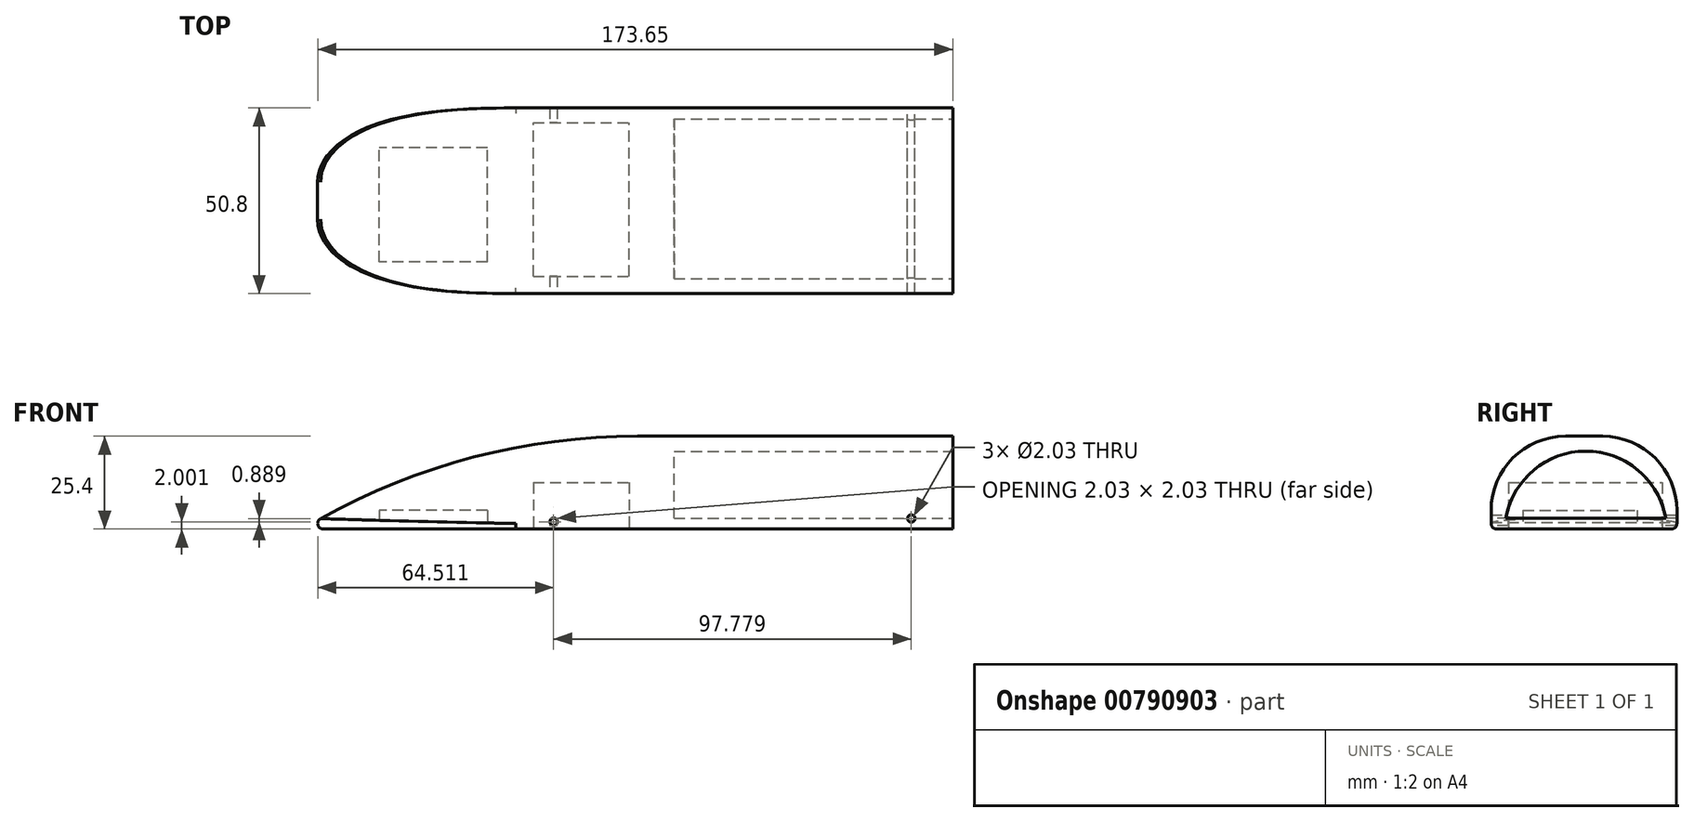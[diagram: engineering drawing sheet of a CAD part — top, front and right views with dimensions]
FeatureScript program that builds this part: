
annotation { "Feature Type Name" : "Feature", "Feature Type Description" : "" }
export const myFeature = defineFeature(function(context is Context, id is Id, definition is map)
    precondition{}
    {
        {
            var Q0;
            Q0=qCreatedBy(makeId("Top.planeOp"),FACE);
            var sketch = newSketch(context, id + "F0", { "sketchPlane" : qUnion([Q0])});
            skLineSegment(sketch, "E0.bottom", {"start": v(-88.9, -25.4) * mm, "end": v(88.9, -25.4) * mm});
            skLineSegment(sketch, "E0.top", {"start": v(-88.9, 25.4) * mm, "end": v(88.9, 25.4) * mm});
            skLineSegment(sketch, "E0.left", {"start": v(-88.9, -25.4) * mm, "end": v(-88.9, 25.4) * mm});
            skLineSegment(sketch, "E0.right", {"start": v(88.9, -25.4) * mm, "end": v(88.9, 25.4) * mm});
            skPoint(sketch, "E0.middle", {"position": v(0, 0) * mm});
            skSolve(sketch);
        }
        {
            var Q0;
            Q0=makeQuery(id+"F0.imprint","IMPRINT",FACE,{"disambiguationData":[TD([[makeQuery(id+"F0.imprint","IMPRINT",EDGE,{"derivedFrom":sQuery(id+"F0.wireOp",EDGE,"E0.bottom")}),1.0]])]});
            extrude(context, id + "F1", {"entities" : qUnion([Q0]), "depth" : 25.4 * mm, "offsetDistance" : 25.4 * mm});
        }
        {
            var Q0;
            Q0=makeQuery(id+"F1.opExtrude","CAP_EDGE",EDGE,{"disambiguationData":[OSD([sQuery(id+"F0.wireOp",EDGE,"E0.left")])],"isStart":false});
            fillet(context, id + "F2", {"entities" : qUnion([Q0]), "radius" : 177.8 * mm, "tangentPropagation" : true, "allowEdgeOverflow" : false});
        }
        {
            var Q0;
            Q0=makeQuery(id+"F2.opFillet","BLEND_EDGE",EDGE,{"blendedFrom":[makeQuery(id+"F1.opExtrude","CAP_EDGE",EDGE,{"disambiguationData":[OSD([sQuery(id+"F0.wireOp",EDGE,"E0.left")])],"isStart":false}),makeQuery(id+"F1.opExtrude","SWEPT_FACE",FACE,{"disambiguationData":[OSD([sQuery(id+"F0.wireOp",EDGE,"E0.top")])]})],"blendedInto":[makeQuery(id+"F1.opExtrude","SWEPT_FACE",FACE,{"disambiguationData":[OSD([sQuery(id+"F0.wireOp",EDGE,"E0.top")])]})]});
            var Q1;
            Q1=makeQuery(id+"F2.opFillet","BLEND_EDGE",EDGE,{"blendedFrom":[makeQuery(id+"F1.opExtrude","CAP_EDGE",EDGE,{"disambiguationData":[OSD([sQuery(id+"F0.wireOp",EDGE,"E0.left")])],"isStart":false}),makeQuery(id+"F1.opExtrude","SWEPT_FACE",FACE,{"disambiguationData":[OSD([sQuery(id+"F0.wireOp",EDGE,"E0.bottom")])]})],"blendedInto":[makeQuery(id+"F1.opExtrude","SWEPT_FACE",FACE,{"disambiguationData":[OSD([sQuery(id+"F0.wireOp",EDGE,"E0.bottom")])]})]});
            fillet(context, id + "F3", {"entities" : qUnion([Q0, Q1]), "radius" : 20.32 * mm, "tangentPropagation" : true, "allowEdgeOverflow" : false});
        }
        {
            var Q0;
            Q0=makeQuery(id+"F1.opExtrude","SWEPT_FACE",FACE,{"disambiguationData":[OSD([sQuery(id+"F0.wireOp",EDGE,"E0.right")])]});
            var sketch = newSketch(context, id + "F4", { "sketchPlane" : qUnion([Q0])});
            skLineSegment(sketch, "E1", {"start": v(-21.36, 2.9) * mm, "end": v(22.36, 2.9) * mm});
            skArc(sketch, "E2", {"start": v(22.36, 2.9) * mm, "mid": v(0.5, 21.3) * mm, "end": v(-21.36, 2.9) * mm});
            skSolve(sketch);
        }
        {
            var Q0;
            Q0=makeQuery(id+"F4.imprint","IMPRINT",FACE,{"disambiguationData":[TD([[makeQuery(id+"F4.imprint","IMPRINT",EDGE,{"derivedFrom":sQuery(id+"F4.wireOp",EDGE,"E1")}),1.0]])]});
            extrude(context, id + "F5", {"entities" : qUnion([Q0]), "operationType" : NewBodyOperationType.REMOVE, "oppositeDirection" : true, "depth" : 76.2 * mm, "offsetDistance" : 25.4 * mm});
        }
        {
            var Q0;
            Q0=makeQuery(id+"F1.opExtrude","SWEPT_FACE",FACE,{"disambiguationData":[OSD([sQuery(id+"F0.wireOp",EDGE,"E0.top")])]});
            var sketch = newSketch(context, id + "F6", { "sketchPlane" : qUnion([Q0])});
            skLineSegment(sketch, "E3", {"start": v(-1.86, 0) * mm, "end": v(-1.86, 1.27) * mm});
            skLineSegment(sketch, "E4", {"start": v(-1.86, 1.27) * mm, "end": v(-1.36, 1.27) * mm});
            skLineSegment(sketch, "E5", {"start": v(-1.36, 1.27) * mm, "end": v(-1.36, 0) * mm});
            skCircle(sketch, "E6", {"center": v(-76.77, 1.63) * mm, "radius": 1.02 * mm});
            skSolve(sketch);
        }
        {
            var Q0;
            {var subQ0=sQuery(id+"F6.wireOp",EDGE,"uXS108uW-j9nu-jN9d-v9bI-wBNLfCoZ4Cw1");Q0=makeQuery(id+"F6.imprint","IMPRINT",FACE,{"disambiguationData":[TD([[makeQuery(id+"F6.imprint","IMPRINT",EDGE,{"derivedFrom":subQ0}),-1.0]])]});}
            var Q1;
            {var subQ0=sQuery(id+"F6.wireOp",EDGE,"E3");Q1=makeQuery(id+"F6.imprint","IMPRINT",FACE,{"disambiguationData":[TD([[makeQuery(id+"F6.imprint","IMPRINT",EDGE,{"derivedFrom":subQ0}),-1.0]])]});}
            extrude(context, id + "F7", {"entities" : qUnion([Q0, Q1]), "operationType" : NewBodyOperationType.REMOVE, "oppositeDirection" : true, "depth" : 76.2 * mm, "offsetDistance" : 25.4 * mm});
        }
        {
            var Q0;
            Q0=makeQuery(id+"F7.boolean.opBoolean","COPY",FACE,{"derivedFrom":makeQuery(id+"F7.opExtrude","SWEPT_FACE",FACE,{"disambiguationData":[OSD([sQuery(id+"F6.wireOp",EDGE,"E5")])]})});
            extrude(context, id + "F8", {"entities" : qUnion([Q0]), "operationType" : NewBodyOperationType.ADD, "depth" : 25.4 * mm, "offsetDistance" : 25.4 * mm});
        }
        {
            var Q0;
            {var subQ0=sQuery(id+"F0.wireOp",EDGE,"E0.bottom");Q0=makeQuery(id+"F8.boolean.opBoolean","MERGE",FACE,{"derivedFrom":[makeQuery(id+"F1.opExtrude","SWEPT_FACE",FACE,{"disambiguationData":[OSD([subQ0])]}),makeQuery(id+"F8.opExtrude","SWEPT_FACE",FACE,{"disambiguationData":[OSD([subQ0,sQuery(id+"F6.wireOp",EDGE,"E5")])]})]});}
            var sketch = newSketch(context, id + "F9", { "sketchPlane" : qUnion([Q0])});
            skCircle(sketch, "E7", {"center": v(-20.24, 2) * mm, "radius": 1.02 * mm});
            skSolve(sketch);
        }
        {
            var Q0;
            Q0=makeQuery(id+"F9.imprint","IMPRINT",FACE,{"disambiguationData":[TD([[makeQuery(id+"F9.imprint","IMPRINT",EDGE,{"derivedFrom":sQuery(id+"F9.wireOp",EDGE,"mDFF4wp4-3rxd-4lJ0-i7Zv-oxogMf14aoRF")}),-1.0]])]});
            var Q1;
            Q1=makeQuery(id+"F9.imprint","IMPRINT",FACE,{"disambiguationData":[TD([[makeQuery(id+"F9.imprint","IMPRINT",EDGE,{"derivedFrom":sQuery(id+"F9.wireOp",EDGE,"E7")}),1.0]])]});
            extrude(context, id + "F10", {"entities" : qUnion([Q0, Q1]), "operationType" : NewBodyOperationType.REMOVE, "oppositeDirection" : true, "depth" : 76.2 * mm, "offsetDistance" : 25.4 * mm});
        }
        {
            var Q0;
            {var subQ0=makeQuery(id+"F7.opExtrude","SWEPT_FACE",FACE,{"disambiguationData":[OSD([sQuery(id+"F6.wireOp",EDGE,"6qoV6KTl-cau2-LcCE-7geX-YWWIEY5zHagg")])]});var subQ1=sQuery(id+"F6.wireOp",EDGE,"E5");var subQ2=sQuery(id+"F0.wireOp",EDGE,"E0.top");var subQ4=sQuery(id+"F0.wireOp",EDGE,"E0.bottom");var subQ6=sQuery(id+"F0.wireOp",EDGE,"E0.left");var subQ7=makeQuery(id+"F1.opExtrude","CAP_FACE",FACE,{"disambiguationData":[OSD([subQ4,subQ2,subQ6,sQuery(id+"F0.wireOp",EDGE,"E0.right")])],"isStart":true});Q0=makeQuery(id+"F10.boolean.opBoolean","SPLIT",FACE,{"disambiguationData":[TD([makeQuery(id+"F7.boolean.opBoolean","COPY",FACE,{"derivedFrom":subQ0})])],"derivedFrom":makeQuery(id+"F8.boolean.opBoolean","MERGE",FACE,{"derivedFrom":[makeQuery(id+"F7.boolean.opBoolean","SPLIT",FACE,{"disambiguationData":[TD([makeQuery(id+"F2.opFillet","BLEND_FACE",FACE,{"disambiguationData":[OSD([subQ6])]})])],"derivedFrom":subQ7}),makeQuery(id+"F7.boolean.opBoolean","SPLIT",FACE,{"disambiguationData":[TD([subQ0])],"derivedFrom":subQ7}),makeQuery(id+"F8.opExtrude","SWEPT_FACE",FACE,{"disambiguationData":[OSD([subQ2,subQ1])]})]})});}
            var sketch = newSketch(context, id + "F11", { "sketchPlane" : qUnion([Q0])});
            skLineSegment(sketch, "E8.bottom", {"start": v(-25.8, 20.65) * mm, "end": v(-5.9, 20.65) * mm});
            skLineSegment(sketch, "E8.top", {"start": v(-25.8, -21.39) * mm, "end": v(-5.9, -21.39) * mm});
            skLineSegment(sketch, "E8.left", {"start": v(-25.8, 20.65) * mm, "end": v(-25.8, -21.39) * mm});
            skLineSegment(sketch, "E8.right", {"start": v(-5.9, 20.65) * mm, "end": v(-5.9, -21.39) * mm});
            skSolve(sketch);
        }
        {
            var Q0;
            Q0=makeQuery(id+"F11.imprint","IMPRINT",FACE,{"disambiguationData":[TD([[makeQuery(id+"F11.imprint","IMPRINT",EDGE,{"derivedFrom":sQuery(id+"F11.wireOp",EDGE,"E8.bottom")}),-1.0]])]});
            extrude(context, id + "F12", {"entities" : qUnion([Q0]), "operationType" : NewBodyOperationType.REMOVE, "oppositeDirection" : true, "depth" : 12.7 * mm, "offsetDistance" : 25.4 * mm});
        }
        {
            var Q0;
            {var subQ0=sQuery(id+"F0.wireOp",EDGE,"E0.left");var subQ1=sQuery(id+"F0.wireOp",EDGE,"E0.bottom");var subQ3=makeQuery(id+"F2.opFillet","BLEND_FACE",FACE,{"disambiguationData":[OSD([subQ0])]});var subQ4=sQuery(id+"F0.wireOp",EDGE,"E0.top");var subQ6=sQuery(id+"F6.wireOp",EDGE,"E5");var subQ9=makeQuery(id+"F1.opExtrude","CAP_FACE",FACE,{"disambiguationData":[OSD([subQ1,subQ4,subQ0,sQuery(id+"F0.wireOp",EDGE,"E0.right")])],"isStart":true});Q0=makeQuery(id+"F10.boolean.opBoolean","SPLIT",FACE,{"disambiguationData":[TD([subQ3])],"derivedFrom":makeQuery(id+"F8.boolean.opBoolean","MERGE",FACE,{"derivedFrom":[makeQuery(id+"F7.boolean.opBoolean","SPLIT",FACE,{"disambiguationData":[TD([subQ3])],"derivedFrom":subQ9}),makeQuery(id+"F7.boolean.opBoolean","SPLIT",FACE,{"disambiguationData":[TD([makeQuery(id+"F7.opExtrude","SWEPT_FACE",FACE,{"disambiguationData":[OSD([sQuery(id+"F6.wireOp",EDGE,"6qoV6KTl-cau2-LcCE-7geX-YWWIEY5zHagg")])]})])],"derivedFrom":subQ9}),makeQuery(id+"F8.opExtrude","SWEPT_FACE",FACE,{"disambiguationData":[OSD([subQ4,subQ6])]})]})});}
            var sketch = newSketch(context, id + "F13", { "sketchPlane" : qUnion([Q0])});
            skLineSegment(sketch, "E9.bottom", {"start": v(-38.35, 16.72) * mm, "end": v(-67.96, 16.72) * mm});
            skLineSegment(sketch, "E9.top", {"start": v(-38.35, -14.52) * mm, "end": v(-67.96, -14.52) * mm});
            skLineSegment(sketch, "E9.left", {"start": v(-38.35, 16.72) * mm, "end": v(-38.35, -14.52) * mm});
            skLineSegment(sketch, "E9.right", {"start": v(-67.96, 16.72) * mm, "end": v(-67.96, -14.52) * mm});
            skSolve(sketch);
        }
        {
            var Q0;
            Q0=makeQuery(id+"F13.imprint","IMPRINT",FACE,{"disambiguationData":[TD([[makeQuery(id+"F13.imprint","IMPRINT",EDGE,{"derivedFrom":sQuery(id+"F13.wireOp",EDGE,"E9.bottom")}),1.0]])]});
            extrude(context, id + "F14", {"entities" : qUnion([Q0]), "operationType" : NewBodyOperationType.REMOVE, "oppositeDirection" : true, "depth" : 5.08 * mm, "offsetDistance" : 25.4 * mm});
        }
        {
            var Q0;
            Q0=makeQuery(id+"F12.boolean.opBoolean","COPY",FACE,{"derivedFrom":makeQuery(id+"F12.opExtrude","SWEPT_FACE",FACE,{"disambiguationData":[OSD([sQuery(id+"F11.wireOp",EDGE,"E8.right")])]})});
            extrude(context, id + "F15", {"entities" : qUnion([Q0]), "operationType" : NewBodyOperationType.REMOVE, "oppositeDirection" : true, "depth" : 6.35 * mm, "offsetDistance" : 25.4 * mm});
        }
        {
            var Q0;
            {var subQ0=sQuery(id+"F0.wireOp",EDGE,"E0.left");var subQ1=sQuery(id+"F0.wireOp",EDGE,"E0.top");Q0=makeQuery(id+"F3.opFillet","BLEND_EDGE",EDGE,{"blendedFrom":[makeQuery(id+"F2.opFillet","BLEND_EDGE",EDGE,{"blendedFrom":[makeQuery(id+"F1.opExtrude","CAP_EDGE",EDGE,{"disambiguationData":[OSD([subQ0])],"isStart":false}),makeQuery(id+"F1.opExtrude","SWEPT_FACE",FACE,{"disambiguationData":[OSD([subQ1])]})],"blendedInto":[makeQuery(id+"F1.opExtrude","SWEPT_FACE",FACE,{"disambiguationData":[OSD([subQ1])]})]}),makeQuery(id+"F1.opExtrude","CAP_FACE",FACE,{"disambiguationData":[OSD([sQuery(id+"F0.wireOp",EDGE,"E0.bottom"),subQ1,subQ0,sQuery(id+"F0.wireOp",EDGE,"E0.right")])],"isStart":true})],"blendedInto":[makeQuery(id+"F1.opExtrude","CAP_FACE",FACE,{"disambiguationData":[OSD([sQuery(id+"F0.wireOp",EDGE,"E0.bottom"),subQ1,subQ0,sQuery(id+"F0.wireOp",EDGE,"E0.right")])],"isStart":true})]});}
            var Q1;
            {var subQ0=sQuery(id+"F0.wireOp",EDGE,"E0.left");Q1=makeQuery(id+"F2.opFillet","BLEND_EDGE",EDGE,{"blendedFrom":[makeQuery(id+"F1.opExtrude","CAP_EDGE",EDGE,{"disambiguationData":[OSD([subQ0])],"isStart":false}),makeQuery(id+"F1.opExtrude","CAP_FACE",FACE,{"disambiguationData":[OSD([sQuery(id+"F0.wireOp",EDGE,"E0.bottom"),sQuery(id+"F0.wireOp",EDGE,"E0.top"),subQ0,sQuery(id+"F0.wireOp",EDGE,"E0.right")])],"isStart":true})],"blendedInto":[makeQuery(id+"F1.opExtrude","CAP_FACE",FACE,{"disambiguationData":[OSD([sQuery(id+"F0.wireOp",EDGE,"E0.bottom"),sQuery(id+"F0.wireOp",EDGE,"E0.top"),subQ0,sQuery(id+"F0.wireOp",EDGE,"E0.right")])],"isStart":true})]});}
            var Q2;
            {var subQ0=sQuery(id+"F0.wireOp",EDGE,"E0.left");var subQ1=sQuery(id+"F0.wireOp",EDGE,"E0.bottom");Q2=makeQuery(id+"F3.opFillet","BLEND_EDGE",EDGE,{"blendedFrom":[makeQuery(id+"F2.opFillet","BLEND_EDGE",EDGE,{"blendedFrom":[makeQuery(id+"F1.opExtrude","CAP_EDGE",EDGE,{"disambiguationData":[OSD([subQ0])],"isStart":false}),makeQuery(id+"F1.opExtrude","SWEPT_FACE",FACE,{"disambiguationData":[OSD([subQ1])]})],"blendedInto":[makeQuery(id+"F1.opExtrude","SWEPT_FACE",FACE,{"disambiguationData":[OSD([subQ1])]})]}),makeQuery(id+"F1.opExtrude","CAP_FACE",FACE,{"disambiguationData":[OSD([subQ1,sQuery(id+"F0.wireOp",EDGE,"E0.top"),subQ0,sQuery(id+"F0.wireOp",EDGE,"E0.right")])],"isStart":true})],"blendedInto":[makeQuery(id+"F1.opExtrude","CAP_FACE",FACE,{"disambiguationData":[OSD([subQ1,sQuery(id+"F0.wireOp",EDGE,"E0.top"),subQ0,sQuery(id+"F0.wireOp",EDGE,"E0.right")])],"isStart":true})]});}
            fillet(context, id + "F16", {"entities" : qUnion([Q0, Q1, Q2]), "radius" : 1.52 * mm, "tangentPropagation" : true, "allowEdgeOverflow" : false});
        }
        {
            var Q0;
            Q0=makeQuery(id+"F8.boolean.opBoolean","MERGE",FACE,{"derivedFrom":[makeQuery(id+"F1.opExtrude","SWEPT_FACE",FACE,{"disambiguationData":[OSD([sQuery(id+"F0.wireOp",EDGE,"E0.top")])]}),makeQuery(id+"F8.opExtrude","SWEPT_FACE",FACE,{"disambiguationData":[OSD([sQuery(id+"F6.wireOp",EDGE,"E5")])]})]});
            var sketch = newSketch(context, id + "F17", { "sketchPlane" : qUnion([Q0])});
            skCircle(sketch, "E10", {"center": v(-77.54, 2.89) * mm, "radius": 1.02 * mm});
            skSolve(sketch);
        }
        {
            var Q0;
            Q0=makeQuery(id+"F17.imprint","IMPRINT",FACE,{"disambiguationData":[TD([[makeQuery(id+"F17.imprint","IMPRINT",EDGE,{"derivedFrom":sQuery(id+"F17.wireOp",EDGE,"E10")}),1.0]])]});
            extrude(context, id + "F18", {"entities" : qUnion([Q0]), "operationType" : NewBodyOperationType.REMOVE, "oppositeDirection" : true, "depth" : 127 * mm, "offsetDistance" : 25.4 * mm});
        }
    });
